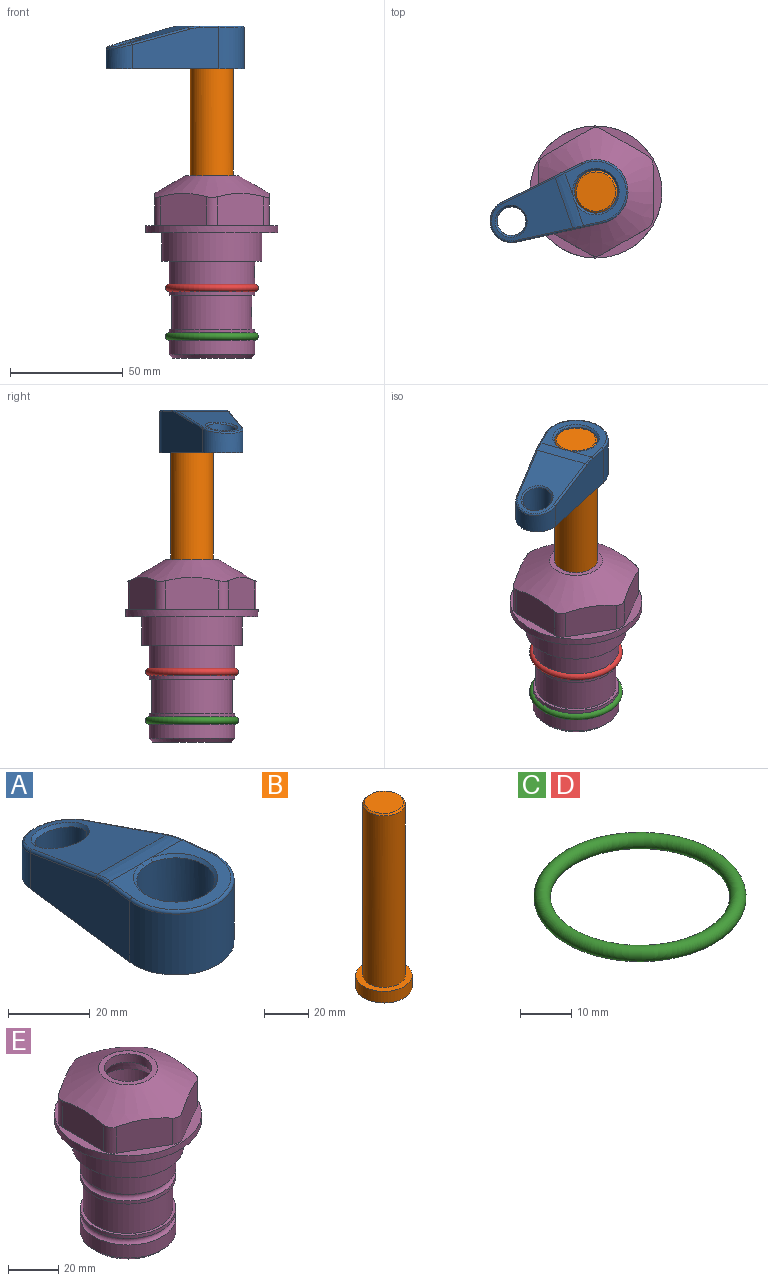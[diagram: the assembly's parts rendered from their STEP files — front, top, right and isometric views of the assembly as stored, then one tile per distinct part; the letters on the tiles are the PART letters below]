
ASSEMBLY  parts=5 mates=4
PART A: 31 faces, bbox 31.7x65.5x19.8 mm
  f0: plane 39.12x18.26mm, normal (0.99,0.12,0), area 612.2mm2, adj f1,f4,f7,f11,f13,f15
  f1: cylinder r=9.53mm len=18.91mm, axis (0,0,-1), area 296.1mm2, adj f0,f2,f7,f17
  f2: plane 39.12x18.26mm, normal (-0.99,0.12,0), area 612.2mm2, adj f1,f4,f7,f12,f14,f16
  f3: cylinder r=6.35mm len=12.7mm, axis (0,0,-1), area 362.4mm2, adj f7,f18
  f4: cylinder r=14.29mm len=28.58mm, axis (0,0,-1), area 882.2mm2, adj f0,f2,f7,f10
  f5: cylinder r=9.53mm len=19.05mm, axis (0,0,-1), area 1092.6mm2, adj f7,f19,f20
  f6: plane 26.99x23.69mm, normal (0,0,1), area 216.2mm2, adj f9,f10,f11,f12,f19
  f7: plane 63.5x28.58mm, normal (0,0,-1), area 661.8mm2, adj f0,f1,f2,f3,f4,f5,f22,f23
  f8: plane 33.52x23.6mm, normal (0,0.26,0.97), area 486mm2, adj f9,f15,f16,f17,f18
  f9: cylinder r=19.05mm len=24.72mm, axis (1,0,0), area 120.4mm2, adj f6,f8,f13,f14,f20
  f10: torus R=13.49mm, axis (0,0,1), area 59mm2, adj f4,f6,f11,f12
  f11: cylinder r=0.79mm len=8.67mm, axis (0.12,-0.99,0), area 10.8mm2, adj f0,f6,f10,f13
  f12: cylinder r=0.79mm len=8.67mm, axis (0.12,0.99,0), area 10.8mm2, adj f2,f6,f10,f14
  f13: bspline ~4.95x1.42mm, area 6.1mm2, adj f0,f9,f11,f15
  f14: bspline ~4.95x1.42mm, area 6.1mm2, adj f2,f9,f12,f16
  f15: cylinder r=0.79mm len=25.95mm, axis (0.12,-0.96,0.26), area 32.9mm2, adj f0,f8,f13,f17
  f16: cylinder r=0.79mm len=25.95mm, axis (0.12,0.96,-0.26), area 32.9mm2, adj f2,f8,f14,f17
  f17: bspline ~18.91x8.38mm, area 30mm2, adj f1,f8,f15,f16
  f18: bspline ~14.29x14.29mm, area 48.3mm2, adj f3,f8
  f19: cone r=9.53mm half-angle=45deg, axis (0,0,1), area 66.5mm2, adj f5,f6,f20
  f20: bspline ~3.22x0.96mm, area 3.5mm2, adj f5,f9,f19
  f21: plane 2.75x2.72mm, normal (0,0,-1), area 2.9mm2, adj f23,f25,f28
  f22: plane 23.05x15.88mm, normal (-0.99,-0.12,0), area 323.6mm2, adj f7,f25,f26,f27,f28,f29
  f23: plane 23.05x15.88mm, normal (0.99,-0.12,0), area 323.6mm2, adj f7,f21,f25,f27,f28,f30
  f24: cylinder r=9.53mm len=10.69mm, axis (0,0,-1), area 114.7mm2, adj f7,f27,f29,f30
  f25: cylinder r=12.7mm len=20.59mm, axis (0,0,-1), area 381.1mm2, adj f7,f21,f22,f23,f26,f28
  f26: plane 2.75x2.72mm, normal (0,0,-1), area 2.9mm2, adj f22,f25,f28
  f27: plane 19.72x18.37mm, normal (0,-0.26,-0.97), area 291.8mm2, adj f22,f23,f24,f28,f29,f30
  f28: cylinder r=15.88mm len=19.92mm, axis (1,0,0), area 54.8mm2, adj f21,f22,f23,f25,f26,f27
  f29: cylinder r=1.59mm len=11mm, axis (0,0,-1), area 34.7mm2, adj f7,f22,f24,f27
  f30: cylinder r=1.59mm len=11mm, axis (0,0,-1), area 34.7mm2, adj f7,f23,f24,f27
PART B: 6 faces, bbox 25.4x25.4x101.6 mm
  f0: plane 17.46x17.46mm, normal (0,0,1), area 239.5mm2, adj f5
  f1: plane 25.4x25.4mm, normal (0,0,-1), area 506.7mm2, adj f2
  f2: cylinder r=12.7mm len=25.4mm, axis (0,0,1), area 506.7mm2, adj f1,f3
  f3: plane 25.4x25.4mm, normal (0,0,1), area 221.7mm2, adj f2,f4
  f4: cylinder r=9.53mm len=94.46mm, axis (0,0,1), area 5653mm2, adj f3,f5
  f5: cone r=8.73mm half-angle=45deg, axis (0,0,-1), area 64.4mm2, adj f0,f4
PART C: 1 faces, bbox 44.7x44.7x3.2 mm
  f0: torus R=19.05mm, axis (0,0,1), area 1193.9mm2
PART D: same geometry as C
PART E: 36 faces, bbox 58.7x58.7x81 mm
  f0: cylinder r=17.78mm len=35.56mm, axis (0,0,1), area 1670.8mm2, adj f23,f24,f31
  f1: cylinder r=19.05mm len=38.1mm, axis (0,0,1), area 1191.9mm2, adj f26,f27,f30
  f2: plane 58.66x58.66mm, normal (0,0,-1), area 1150.6mm2, adj f3,f28
  f3: cylinder r=29.33mm len=58.66mm, axis (0,0,-1), area 585.1mm2, adj f2,f4
  f4: plane 58.66x58.66mm, normal (0,0,1), area 475.9mm2, adj f3,f5,f6,f7,f8,f9,f10,f11
  f5: plane 20.32x14.34mm, normal (-0.5,0.87,0), area 324.4mm2, adj f4,f15,f16,f17
  f6: plane 20.32x14.34mm, normal (0.5,0.87,0), area 324.4mm2, adj f4,f14,f15,f17
  f7: plane 23.48x14.34mm, normal (1,0,0), area 324.4mm2, adj f4,f13,f14,f17
  f8: plane 20.32x14.34mm, normal (0.5,-0.87,0), area 324.4mm2, adj f4,f12,f13,f17
  f9: plane 20.32x14.34mm, normal (-0.5,-0.87,0), area 324.4mm2, adj f4,f11,f12,f17
  f10: plane 23.48x14.34mm, normal (-1,0,0), area 324.4mm2, adj f4,f11,f16,f17
  f11: cylinder r=5.08mm len=12.85mm, axis (0,0,-1), area 67.2mm2, adj f4,f9,f10,f17
  f12: cylinder r=5.08mm len=12.85mm, axis (0,0,-1), area 67.2mm2, adj f4,f8,f9,f17
  f13: cylinder r=5.08mm len=12.85mm, axis (0,0,-1), area 67.2mm2, adj f4,f7,f8,f17
  f14: cylinder r=5.08mm len=12.85mm, axis (0,0,-1), area 67.2mm2, adj f4,f6,f7,f17
  f15: cylinder r=5.08mm len=12.85mm, axis (0,0,-1), area 67.2mm2, adj f4,f5,f6,f17
  f16: cylinder r=5.08mm len=12.85mm, axis (0,0,-1), area 67.2mm2, adj f4,f5,f10,f17
  f17: cone r=11.73mm half-angle=60deg, axis (0,0,-1), area 2071.8mm2, adj f5,f6,f7,f8,f9,f10,f11,f12
  f18: plane 23.46x23.46mm, normal (0,0,1), area 147.4mm2, adj f17,f35
  f19: plane 34.93x34.93mm, normal (0,0,-1), area 958mm2, adj f29
  f20: cylinder r=19.05mm len=38.1mm, axis (0,0,1), area 760.1mm2, adj f21,f29
  f21: torus R=19.05mm, axis (0,0,1), area 565.3mm2, adj f20,f22
  f22: cylinder r=19.05mm len=38.1mm, axis (0,0,1), area 190mm2, adj f21,f23
  f23: plane 38.1x38.1mm, normal (0,0,1), area 146.9mm2, adj f0,f22
  f24: plane 38.1x38.1mm, normal (0,0,-1), area 146.9mm2, adj f0,f25
  f25: cylinder r=19.05mm len=38.1mm, axis (0,0,1), area 190mm2, adj f24,f26
  f26: torus R=19.05mm, axis (0,0,1), area 565.3mm2, adj f1,f25
  f27: plane 44.45x44.45mm, normal (0,0,-1), area 411.7mm2, adj f1,f28
  f28: cylinder r=22.23mm len=44.45mm, axis (0,0,1), area 1773.5mm2, adj f2,f27
  f29: cone r=19.05mm half-angle=45deg, axis (0,0,1), area 257.5mm2, adj f19,f20
  f30: cylinder r=3.17mm len=6.75mm, axis (-1,0,0), area 128mm2, adj f1,f33
  f31: cylinder r=3.17mm len=6.35mm, axis (-1,0,0), area 102.5mm2, adj f0,f33
  f32: plane 25.4x25.4mm, normal (0,0,1), area 506.7mm2, adj f33
  f33: cylinder r=12.7mm len=66.42mm, axis (0,0,-1), area 5236.2mm2, adj f30,f31,f32,f34
  f34: cone r=9.53mm half-angle=30deg, axis (0,0,-1), area 443.4mm2, adj f33,f35
  f35: cylinder r=9.53mm len=19.05mm, axis (0,0,-1), area 240.9mm2, adj f18,f34
PLACE A rot(axis=(0,0,1),109.3deg) t=(0,0,28.35)mm
PLACE B rot(axis=(0,0,-1),160.7deg) t=(0,0,27.55)mm
PLACE C t=(0,0,-21.59)mm
PLACE D at identity
PLACE E at identity fixed
MATE fastened C.f0 <-> E.f0  axis (0,0,1) through (0,0,-46.1)mm
MATE fastened D.f0 <-> E.f0  axis (0,0,1) through (0,0,-24.51)mm
MATE cylindrical B.f2 <-> E.f0  axis (0,0,-1) through (0,0,-10.55)mm
MATE fastened B.f2 <-> A.f4  axis (0,0,1) through (0,0,91.05)mm
